# Revit family: Recycling-Waste-Bins_Mezzo_Triple-Waste-Unit_Busch-Systems
name_source: partatom
category: Generic Models
units: mm (PartAtom-declared; Revit-internal decimal feet)

## family parameters
Always vertical = Yes
Can host rebar = No
Cut with Voids When Loaded = No
Maintain Annotation Orientation = No
Part Type = Normal
Room Calculation Point = No
Round Connector Dimension = Use Diameter
Shared = No
Work Plane-Based = No

## types (2) — shared parameters
Body Material = White
Bottom Stud = No
Default Elevation = 0' - 0"
Dimension (H x W x D) = 30.625”H x 39.8125”W x 15”D
Double Frame = No
Keynote = 11 82 00
Manufacturer = Busch Systems International Inc.
Model = MEZZO
Product Page URL = https://www.arcat.com
Text = White
URL = https://www.buschsystems.com
WASTE ONLY = Slate
Wheel = Yes

## per-type parameters (varying)
| type | MIXED RECYCLABLES | ORGANICS | Single Frame | Triple Frame |
| MEZZO - Triple - Ml - Mixed Recyclables-Organics-Waste - Full - White-Blue-Green-Black | Mixed Recyclables | Organics | Yes | No |
| MEZZO - Triple - Hl - Mixed Recyclables-Organics-Waste - Full - White-Black | <By Category> | <By Category> | No | Yes |

note: column(s) folded — value = type name in every type: Product Name

## geometry (parser evidence)
native form markers: Sweep x7
no freeform markers — native parametric forms only
